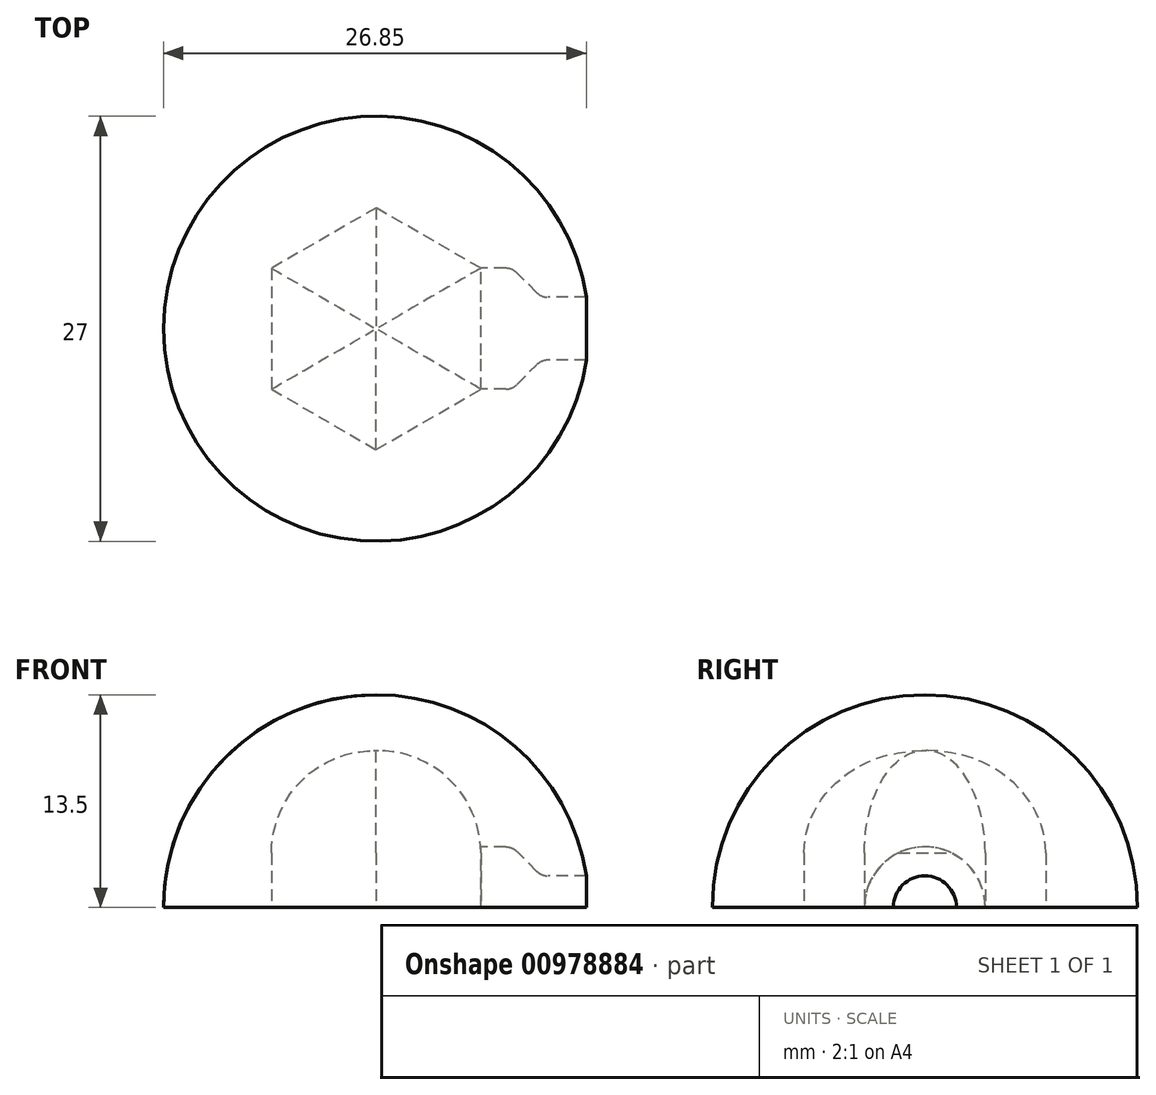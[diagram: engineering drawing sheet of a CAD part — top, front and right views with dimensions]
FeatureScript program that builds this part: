
annotation { "Feature Type Name" : "Feature", "Feature Type Description" : "" }
export const myFeature = defineFeature(function(context is Context, id is Id, definition is map)
    precondition{}
    {
        {
            var Q0;
            Q0=qCreatedBy(makeId("Front.planeOp"),FACE);
            var sketch = newSketch(context, id + "F0", { "sketchPlane" : qUnion([Q0])});
            skArc(sketch, "E0", {"start": v(0, 13.5) * mm, "mid": v(-9.55, 9.55) * mm, "end": v(-13.5, 0) * mm});
            skLineSegment(sketch, "E1", {"start": v(-13.5, 0) * mm, "end": v(0, 0) * mm});
            skLineSegment(sketch, "E2", {"start": v(0, 0) * mm, "end": v(0, 13.5) * mm});
            skSolve(sketch);
        }
        {
            var Q0;
            Q0=makeQuery(id+"F0.imprint","IMPRINT",FACE,{"disambiguationData":[TD([[makeQuery(id+"F0.imprint","IMPRINT",EDGE,{"derivedFrom":sQuery(id+"F0.wireOp",EDGE,"E0")}),1.0]])]});
            var Q1;
            Q1=sQuery(id+"F0.wireOp",EDGE,"E2");
            revolve(context, id + "F1", {"surfaceOperationType" : NewSurfaceOperationType.NEW, "entities" : qUnion([Q0]), "axis" : qUnion([Q1]), "revolveType" : RevolveType.FULL});
        }
        {
            var Q0;
            Q0=makeQuery(id+"F1.opRevolve","SWEPT_FACE",FACE,{"disambiguationData":[OSD([sQuery(id+"F0.wireOp",EDGE,"E1")])]});
            var sketch = newSketch(context, id + "F2", { "sketchPlane" : qUnion([Q0])});
            skCircle(sketch, "E3.cCircle", {"center": v(0, 0) * mm, "radius": 6.65 * mm, "construction": true});
            skLineSegment(sketch, "E3.0", {"start": v(6.65, 3.84) * mm, "end": v(6.65, -3.84) * mm});
            skLineSegment(sketch, "E3.1", {"start": v(6.65, -3.84) * mm, "end": v(0, -7.68) * mm});
            skLineSegment(sketch, "E3.2", {"start": v(0, -7.68) * mm, "end": v(-6.65, -3.84) * mm});
            skLineSegment(sketch, "E3.3", {"start": v(-6.65, -3.84) * mm, "end": v(-6.65, 3.84) * mm});
            skLineSegment(sketch, "E3.4", {"start": v(-6.65, 3.84) * mm, "end": v(0, 7.68) * mm});
            skLineSegment(sketch, "E3.5", {"start": v(0, 7.68) * mm, "end": v(6.65, 3.84) * mm});
            skPoint(sketch, "E3.0.midPoint", {"position": v(6.65, 0) * mm});
            skSolve(sketch);
        }
        {
            var Q0;
            Q0 = qSketchRegion(id + "F2", true);
            extrude(context, id + "F3", {"entities" : qUnion([Q0]), "operationType" : NewBodyOperationType.REMOVE, "oppositeDirection" : true, "depth" : (6.9 / 2 + 6.5) * mm, "offsetDistance" : 25 * mm});
        }
        {
            var Q0;
            Q0=makeQuery(id+"F3.boolean.opBoolean","COPY",FACE,{"derivedFrom":makeQuery(id+"F3.opExtrude","SWEPT_FACE",FACE,{"disambiguationData":[OSD([sQuery(id+"F2.wireOp",EDGE,"E3.0")])]})});
            var sketch = newSketch(context, id + "F4", { "sketchPlane" : qUnion([Q0])});
            skArc(sketch, "E4", {"start": v(2, 0) * mm, "mid": v(0, 2) * mm, "end": v(-2, 0) * mm});
            skSolve(sketch);
        }
        {
            var Q0;
            {var subQ0=sQuery(id+"F4.wireOp",EDGE,"E4");Q0=makeQuery(id+"F4.imprint","IMPRINT",FACE,{"disambiguationData":[TD([[makeQuery(id+"F4.imprint","IMPRINT",EDGE,{"derivedFrom":subQ0}),1.0]])]});}
            extrude(context, id + "F5", {"entities" : qUnion([Q0]), "operationType" : NewBodyOperationType.REMOVE, "endBound" : BoundingType.THROUGH_ALL, "oppositeDirection" : true, "depth" : 25 * mm, "offsetDistance" : 25 * mm});
        }
        {
            var Q0;
            Q0=makeQuery(id+"F3.boolean.opBoolean","COPY",EDGE,{"derivedFrom":makeQuery(id+"F3.opExtrude","CAP_EDGE",EDGE,{"disambiguationData":[OSD([sQuery(id+"F2.wireOp",EDGE,"E3.0")])],"isStart":false})});
            var Q1;
            Q1=makeQuery(id+"F3.boolean.opBoolean","COPY",EDGE,{"derivedFrom":makeQuery(id+"F3.opExtrude","CAP_EDGE",EDGE,{"disambiguationData":[OSD([sQuery(id+"F2.wireOp",EDGE,"E3.1")])],"isStart":false})});
            var Q2;
            Q2=makeQuery(id+"F3.boolean.opBoolean","COPY",EDGE,{"derivedFrom":makeQuery(id+"F3.opExtrude","CAP_EDGE",EDGE,{"disambiguationData":[OSD([sQuery(id+"F2.wireOp",EDGE,"E3.2")])],"isStart":false})});
            var Q3;
            Q3=makeQuery(id+"F3.boolean.opBoolean","COPY",EDGE,{"derivedFrom":makeQuery(id+"F3.opExtrude","CAP_EDGE",EDGE,{"disambiguationData":[OSD([sQuery(id+"F2.wireOp",EDGE,"E3.3")])],"isStart":false})});
            var Q4;
            Q4=makeQuery(id+"F3.boolean.opBoolean","COPY",EDGE,{"derivedFrom":makeQuery(id+"F3.opExtrude","CAP_EDGE",EDGE,{"disambiguationData":[OSD([sQuery(id+"F2.wireOp",EDGE,"E3.4")])],"isStart":false})});
            var Q5;
            Q5=makeQuery(id+"F3.boolean.opBoolean","COPY",EDGE,{"derivedFrom":makeQuery(id+"F3.opExtrude","CAP_EDGE",EDGE,{"disambiguationData":[OSD([sQuery(id+"F2.wireOp",EDGE,"E3.5")])],"isStart":false})});
            fillet(context, id + "F6", {"entities" : qUnion([Q0, Q1, Q2, Q3, Q4, Q5]), "radius" : 6.5 * mm, "tangentPropagation" : true, "allowEdgeOverflow" : false});
        }
        {
            var Q0;
            Q0=makeQuery(id+"F3.boolean.opBoolean","COPY",FACE,{"derivedFrom":makeQuery(id+"F3.opExtrude","SWEPT_FACE",FACE,{"disambiguationData":[OSD([sQuery(id+"F2.wireOp",EDGE,"E3.0")])]})});
            var sketch = newSketch(context, id + "F7", { "sketchPlane" : qUnion([Q0])});
            skArc(sketch, "E5", {"start": v(3.84, 0) * mm, "mid": v(0, 3.84) * mm, "end": v(-3.84, 0) * mm});
            skPoint(sketch, "E6.0", {"position": v(3.84, 0) * mm});
            skLineSegment(sketch, "E7", {"start": v(3.84, 0) * mm, "end": v(-3.84, 0) * mm});
            skSolve(sketch);
        }
        {
            var Q0;
            Q0 = qSketchRegion(id + "F7", true);
            extrude(context, id + "F8", {"entities" : qUnion([Q0]), "operationType" : NewBodyOperationType.REMOVE, "oppositeDirection" : true, "depth" : 4 * mm, "offsetDistance" : 25 * mm});
        }
        {
            var Q0;
            Q0=makeQuery(id+"F8.boolean.opBoolean","COPY",EDGE,{"derivedFrom":makeQuery(id+"F8.opExtrude","CAP_EDGE",EDGE,{"disambiguationData":[OSD([sQuery(id+"F7.wireOp",EDGE,"E5")])],"isStart":false})});
            chamfer(context, id + "F9", {"entities" : qUnion([Q0]), "width" : 2 * mm, "tangentPropagation" : true});
        }
        {
            var Q0;
            Q0=makeQuery(id+"F9.opChamfer","BLEND_EDGE",EDGE,{"blendedFrom":[makeQuery(id+"F8.boolean.opBoolean","COPY",EDGE,{"derivedFrom":makeQuery(id+"F8.opExtrude","CAP_EDGE",EDGE,{"disambiguationData":[OSD([sQuery(id+"F7.wireOp",EDGE,"E5")])],"isStart":false})}),makeQuery(id+"F5.boolean.opBoolean","COPY",FACE,{"derivedFrom":makeQuery(id+"F5.opExtrude","SWEPT_FACE",FACE,{"disambiguationData":[OSD([sQuery(id+"F4.wireOp",EDGE,"E4")])]})})],"blendedInto":[makeQuery(id+"F5.boolean.opBoolean","COPY",FACE,{"derivedFrom":makeQuery(id+"F5.opExtrude","SWEPT_FACE",FACE,{"disambiguationData":[OSD([sQuery(id+"F4.wireOp",EDGE,"E4")])]})})]});
            var Q1;
            {var subQ0=sQuery(id+"F7.wireOp",EDGE,"E5");Q1=makeQuery(id+"F9.opChamfer","BLEND_EDGE",EDGE,{"blendedFrom":[makeQuery(id+"F8.boolean.opBoolean","COPY",EDGE,{"derivedFrom":makeQuery(id+"F8.opExtrude","CAP_EDGE",EDGE,{"disambiguationData":[OSD([subQ0])],"isStart":false})}),makeQuery(id+"F8.boolean.opBoolean","COPY",FACE,{"derivedFrom":makeQuery(id+"F8.opExtrude","SWEPT_FACE",FACE,{"disambiguationData":[OSD([subQ0])]})})],"blendedInto":[makeQuery(id+"F8.boolean.opBoolean","COPY",FACE,{"derivedFrom":makeQuery(id+"F8.opExtrude","SWEPT_FACE",FACE,{"disambiguationData":[OSD([subQ0])]})})]});}
            var Q2;
            Q2=makeQuery(id+"F3.boolean.opBoolean","COPY",EDGE,{"derivedFrom":makeQuery(id+"F3.opExtrude","CAP_EDGE",EDGE,{"disambiguationData":[OSD([sQuery(id+"F2.wireOp",EDGE,"E3.4")])],"isStart":true})});
            var Q3;
            Q3=makeQuery(id+"F3.boolean.opBoolean","COPY",EDGE,{"derivedFrom":makeQuery(id+"F3.opExtrude","CAP_EDGE",EDGE,{"disambiguationData":[OSD([sQuery(id+"F2.wireOp",EDGE,"E3.5")])],"isStart":true})});
            var Q4;
            Q4=makeQuery(id+"F3.boolean.opBoolean","COPY",EDGE,{"derivedFrom":makeQuery(id+"F3.opExtrude","CAP_EDGE",EDGE,{"disambiguationData":[OSD([sQuery(id+"F2.wireOp",EDGE,"E3.1")])],"isStart":true})});
            var Q5;
            Q5=makeQuery(id+"F3.boolean.opBoolean","COPY",EDGE,{"derivedFrom":makeQuery(id+"F3.opExtrude","CAP_EDGE",EDGE,{"disambiguationData":[OSD([sQuery(id+"F2.wireOp",EDGE,"E3.2")])],"isStart":true})});
            var Q6;
            Q6=makeQuery(id+"F3.boolean.opBoolean","COPY",EDGE,{"derivedFrom":makeQuery(id+"F3.opExtrude","CAP_EDGE",EDGE,{"disambiguationData":[OSD([sQuery(id+"F2.wireOp",EDGE,"E3.3")])],"isStart":true})});
            fillet(context, id + "F10", {"entities" : qUnion([Q0, Q1, Q2, Q3, Q4, Q5, Q6]), "radius" : 1 * mm, "tangentPropagation" : true, "allowEdgeOverflow" : false});
        }
    });
